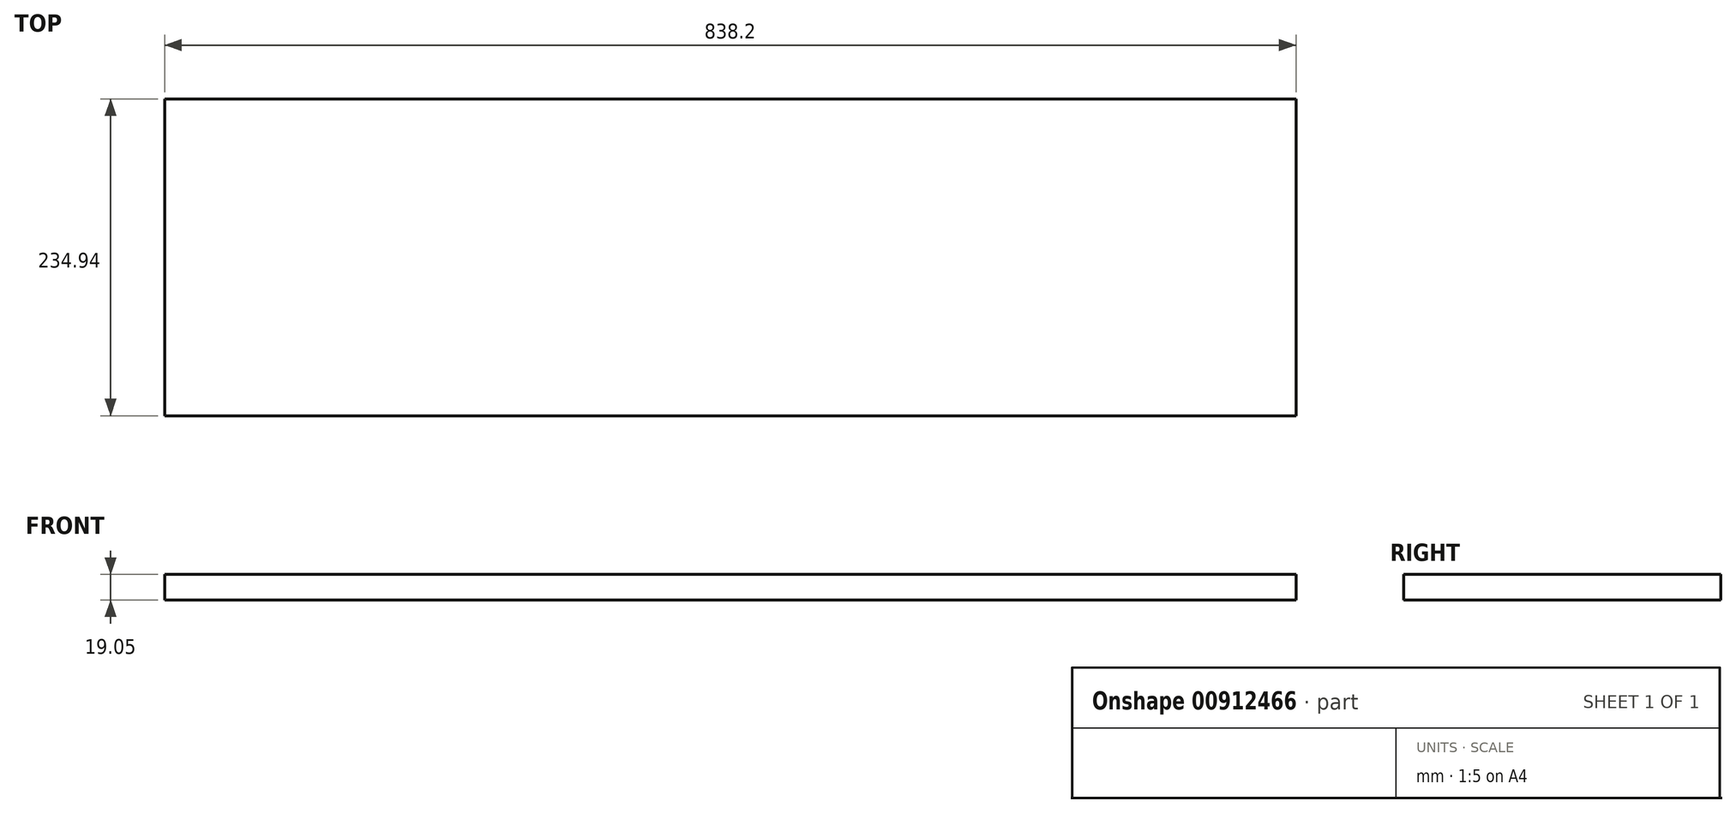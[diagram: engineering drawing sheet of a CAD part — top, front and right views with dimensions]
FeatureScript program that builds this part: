
annotation { "Feature Type Name" : "Feature", "Feature Type Description" : "" }
export const myFeature = defineFeature(function(context is Context, id is Id, definition is map)
    precondition{}
    {
        {
            var Q0;
            Q0=qCreatedBy(makeId("Top.planeOp"),FACE);
            var sketch = newSketch(context, id + "F0", { "sketchPlane" : qUnion([Q0])});
            skLineSegment(sketch, "E0.bottom", {"start": v(419.1, 117.48) * mm, "end": v(-419.1, 117.48) * mm});
            skLineSegment(sketch, "E0.top", {"start": v(419.1, -117.47) * mm, "end": v(-419.1, -117.48) * mm});
            skLineSegment(sketch, "E0.left", {"start": v(419.1, 117.48) * mm, "end": v(419.1, -117.47) * mm});
            skLineSegment(sketch, "E0.right", {"start": v(-419.1, 117.48) * mm, "end": v(-419.1, -117.48) * mm});
            skPoint(sketch, "E0.middle", {"position": v(0, 0) * mm});
            skSolve(sketch);
        }
        {
            var Q0;
            Q0 = qSketchRegion(id + "F0", true);
            extrude(context, id + "F1", {"entities" : qUnion([Q0]), "depth" : 19.05 * mm, "offsetDistance" : 25.4 * mm});
        }
    });
